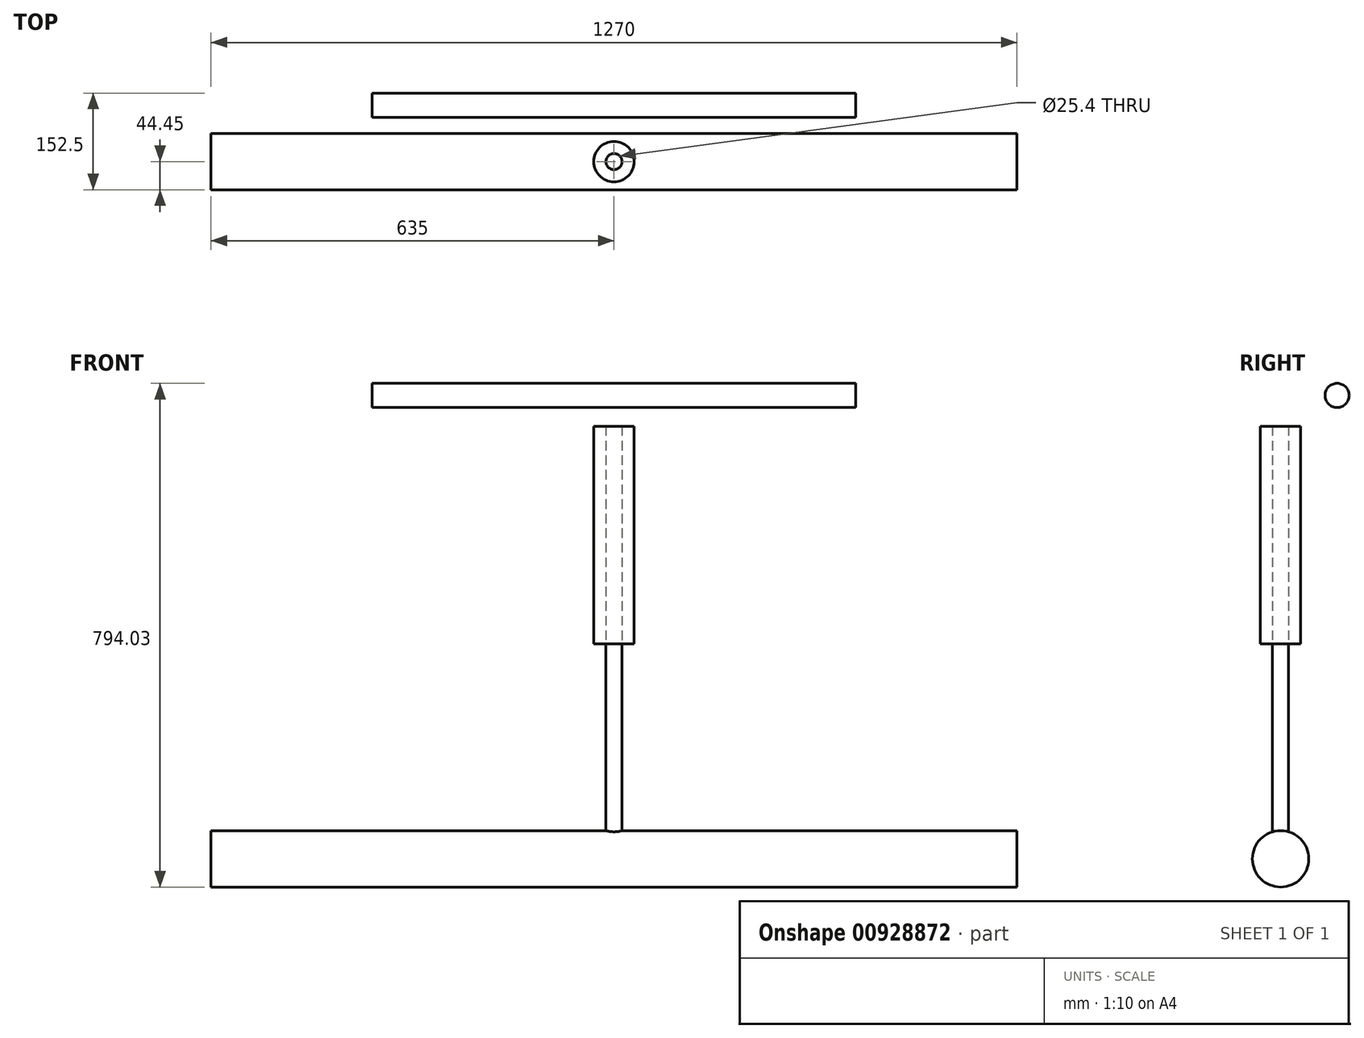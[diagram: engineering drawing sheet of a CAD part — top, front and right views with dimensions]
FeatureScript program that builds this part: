
annotation { "Feature Type Name" : "Feature", "Feature Type Description" : "" }
export const myFeature = defineFeature(function(context is Context, id is Id, definition is map)
    precondition{}
    {
        {
            var Q0;
            Q0=qCreatedBy(makeId("Top.planeOp"),FACE);
            var sketch = newSketch(context, id + "F0", { "sketchPlane" : qUnion([Q0])});
            skCircle(sketch, "E0", {"center": v(0, 0) * mm, "radius": 31.75 * mm});
            skCircle(sketch, "E1", {"center": v(0, 0) * mm, "radius": 12.7 * mm});
            skSolve(sketch);
        }
        {
            var Q0;
            Q0=makeQuery(id+"F0.imprint","IMPRINT",FACE,{"disambiguationData":[TD([[makeQuery(id+"F0.imprint","IMPRINT",EDGE,{"derivedFrom":sQuery(id+"F0.wireOp",EDGE,"E0")}),1.0]])]});
            extrude(context, id + "F1", {"entities" : qUnion([Q0]), "depth" : 342.9 * mm, "offsetDistance" : 25.4 * mm});
        }
        {
            var Q0;
            Q0=makeQuery(id+"F0.imprint","IMPRINT",FACE,{"disambiguationData":[TD([[makeQuery(id+"F0.imprint","IMPRINT",EDGE,{"derivedFrom":sQuery(id+"F0.wireOp",EDGE,"E1")}),1.0]])]});
            var Q1;
            Q1=sQuery(id+"F0.wireOp",EDGE,"E1");
            extrude(context, id + "F2", {"entities" : qUnion([Q0]), "surfaceEntities" : qUnion([Q1]), "oppositeDirection" : true, "depth" : 304.8 * mm, "offsetDistance" : 25.4 * mm});
        }
        {
            var Q0;
            Q0=qCreatedBy(makeId("Right.planeOp"),FACE);
            var sketch = newSketch(context, id + "F3", { "sketchPlane" : qUnion([Q0])});
            skCircle(sketch, "E2", {"center": v(0, -338.96) * mm, "radius": 44.45 * mm});
            skSolve(sketch);
        }
        {
            var Q0;
            Q0 = qSketchRegion(id + "F3", true);
            extrude(context, id + "F4", {"entities" : qUnion([Q0]), "depth" : 635 * mm, "offsetDistance" : 25.4 * mm});
        }
        {
            var Q0;
            Q0=makeQuery(id+"F3.imprint","IMPRINT",FACE,{"disambiguationData":[TD([[makeQuery(id+"F3.imprint","IMPRINT",EDGE,{"derivedFrom":sQuery(id+"F3.wireOp",EDGE,"E2")}),1.0]])]});
            var Q1;
            Q1=sQuery(id+"F3.wireOp",EDGE,"E2");
            extrude(context, id + "F5", {"entities" : qUnion([Q0]), "operationType" : NewBodyOperationType.ADD, "surfaceEntities" : qUnion([Q1]), "depth" : -635 * mm, "offsetDistance" : 25.4 * mm});
        }
        {
            var Q0;
            Q0=qCreatedBy(makeId("Right.planeOp"),FACE);
            var sketch = newSketch(context, id + "F6", { "sketchPlane" : qUnion([Q0])});
            skCircle(sketch, "E3", {"center": v(89, 391.57) * mm, "radius": 19.05 * mm});
            skSolve(sketch);
        }
        {
            var Q0;
            Q0=makeQuery(id+"F6.imprint","IMPRINT",FACE,{"disambiguationData":[TD([[makeQuery(id+"F6.imprint","IMPRINT",EDGE,{"derivedFrom":sQuery(id+"F6.wireOp",EDGE,"E3")}),1.0]])]});
            extrude(context, id + "F7", {"entities" : qUnion([Q0]), "depth" : 381 * mm, "offsetDistance" : 25.4 * mm});
        }
        {
            var Q0;
            Q0=makeQuery(id+"F6.imprint","IMPRINT",FACE,{"disambiguationData":[TD([[makeQuery(id+"F6.imprint","IMPRINT",EDGE,{"derivedFrom":sQuery(id+"F6.wireOp",EDGE,"E3")}),1.0]])]});
            extrude(context, id + "F8", {"entities" : qUnion([Q0]), "operationType" : NewBodyOperationType.ADD, "depth" : -381 * mm, "offsetDistance" : 25.4 * mm});
        }
    });
